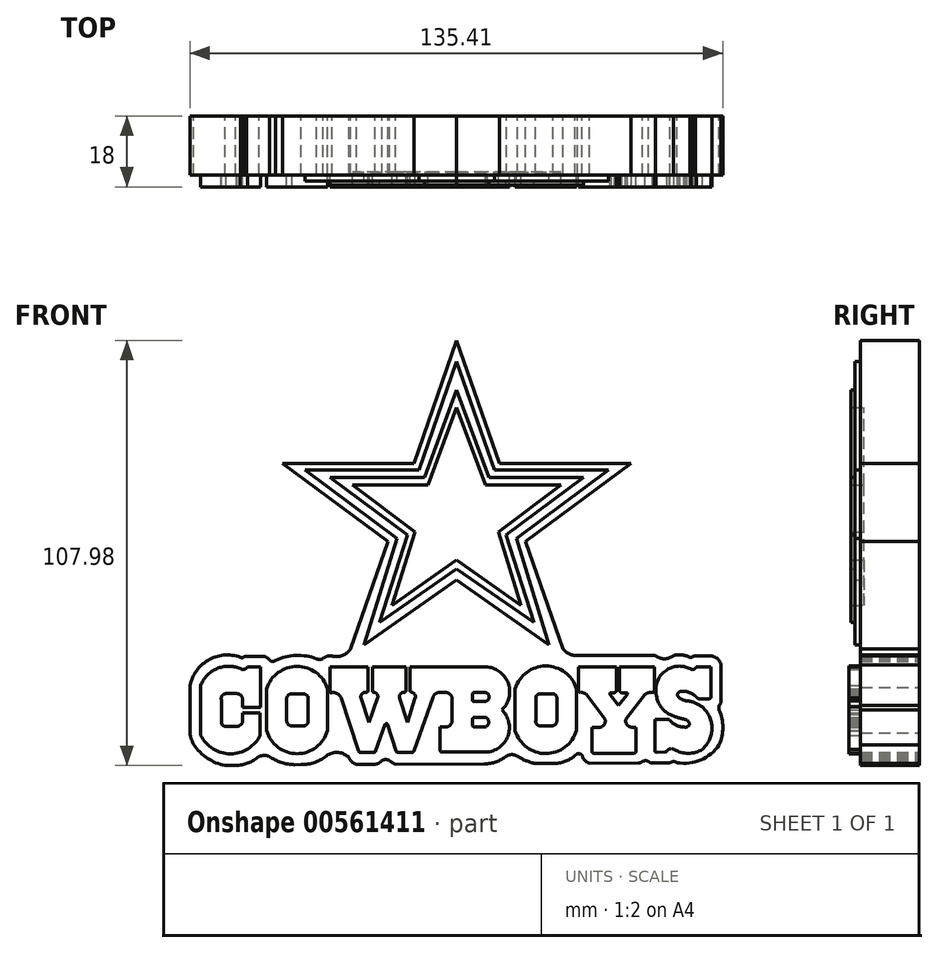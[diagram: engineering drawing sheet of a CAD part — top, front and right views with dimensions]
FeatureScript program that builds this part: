
annotation { "Feature Type Name" : "Feature", "Feature Type Description" : "" }
export const myFeature = defineFeature(function(context is Context, id is Id, definition is map)
    precondition{}
    {
        {
            var Q0;
            Q0=qCreatedBy(makeId("Front.planeOp"),FACE);
            var sketch = newSketch(context, id + "F0", { "sketchPlane" : qUnion([Q0])});
            skLineSegment(sketch, "E0", {"start": v(0, -3.42) * mm, "end": v(-16.39, -14.87) * mm});
            skLineSegment(sketch, "E1", {"start": v(-16.39, -14.87) * mm, "end": v(-10.6, 3.7) * mm});
            skLineSegment(sketch, "E2", {"start": v(-10.6, 3.7) * mm, "end": v(-26.52, 15.64) * mm});
            skLineSegment(sketch, "E3", {"start": v(-26.52, 15.64) * mm, "end": v(-7.34, 15.64) * mm});
            skLineSegment(sketch, "E4", {"start": v(-7.34, 15.64) * mm, "end": v(0, 35.41) * mm});
            skLineSegment(sketch, "E5.MirrorCS", {"start": v(7.34, 15.64) * mm, "end": v(0, 35.41) * mm});
            skLineSegment(sketch, "E6.MirrorCS", {"start": v(26.52, 15.64) * mm, "end": v(7.34, 15.64) * mm});
            skLineSegment(sketch, "E7.MirrorCS", {"start": v(10.6, 3.7) * mm, "end": v(26.52, 15.64) * mm});
            skLineSegment(sketch, "E8.MirrorCS", {"start": v(16.39, -14.87) * mm, "end": v(10.6, 3.7) * mm});
            skLineSegment(sketch, "E9.MirrorCS", {"start": v(0, -3.42) * mm, "end": v(16.39, -14.87) * mm});
            skSolve(sketch);
        }
        {
            var Q0;
            Q0=qCreatedBy(makeId("Front.planeOp"),FACE);
            var sketch = newSketch(context, id + "F1", { "sketchPlane" : qUnion([Q0])});
            skLineSegment(sketch, "E10", {"start": v(0, -5.59) * mm, "end": v(-19.65, -19.21) * mm});
            skLineSegment(sketch, "E11", {"start": v(-19.65, -19.21) * mm, "end": v(-12.53, 2.97) * mm});
            skLineSegment(sketch, "E12", {"start": v(-12.53, 2.97) * mm, "end": v(-32.19, 17.57) * mm});
            skLineSegment(sketch, "E13", {"start": v(-32.19, 17.57) * mm, "end": v(-8.19, 17.57) * mm});
            skLineSegment(sketch, "E14", {"start": v(-8.19, 17.57) * mm, "end": v(0, 39.88) * mm});
            skLineSegment(sketch, "E15.MirrorCS", {"start": v(8.19, 17.57) * mm, "end": v(0, 39.88) * mm});
            skLineSegment(sketch, "E16.MirrorCS", {"start": v(32.19, 17.57) * mm, "end": v(8.19, 17.57) * mm});
            skLineSegment(sketch, "E17.MirrorCS", {"start": v(12.53, 2.97) * mm, "end": v(32.19, 17.57) * mm});
            skLineSegment(sketch, "E18.MirrorCS", {"start": v(19.65, -19.21) * mm, "end": v(12.53, 2.97) * mm});
            skLineSegment(sketch, "E19.MirrorCS", {"start": v(0, -5.59) * mm, "end": v(19.65, -19.21) * mm});
            skSolve(sketch);
        }
        {
            var Q0;
            Q0=qCreatedBy(makeId("Front.planeOp"),FACE);
            var sketch = newSketch(context, id + "F2", { "sketchPlane" : qUnion([Q0])});
            skLineSegment(sketch, "E20", {"start": v(0, -8.48) * mm, "end": v(-23.5, -24.88) * mm});
            skLineSegment(sketch, "E21", {"start": v(-23.5, -24.88) * mm, "end": v(-15.18, 2.13) * mm});
            skLineSegment(sketch, "E22", {"start": v(-15.18, 2.13) * mm, "end": v(-38.58, 19.5) * mm});
            skLineSegment(sketch, "E23", {"start": v(-38.58, 19.5) * mm, "end": v(-9.64, 19.5) * mm});
            skLineSegment(sketch, "E24", {"start": v(-9.64, 19.5) * mm, "end": v(0, 47.11) * mm});
            skLineSegment(sketch, "E25.MirrorCS", {"start": v(9.64, 19.5) * mm, "end": v(0, 47.11) * mm});
            skLineSegment(sketch, "E26.MirrorCS", {"start": v(38.58, 19.5) * mm, "end": v(9.64, 19.5) * mm});
            skLineSegment(sketch, "E27.MirrorCS", {"start": v(15.18, 2.13) * mm, "end": v(38.58, 19.5) * mm});
            skLineSegment(sketch, "E28.MirrorCS", {"start": v(23.5, -24.88) * mm, "end": v(15.18, 2.13) * mm});
            skLineSegment(sketch, "E29.MirrorCS", {"start": v(0, -8.48) * mm, "end": v(23.5, -24.88) * mm});
            skSolve(sketch);
        }
        {
            var Q0;
            Q0=qCreatedBy(makeId("Front.planeOp"),FACE);
            var sketch = newSketch(context, id + "F3", { "sketchPlane" : qUnion([Q0])});
            skLineSegment(sketch, "E30", {"start": v(-17.47, 1.4) * mm, "end": v(-44.25, 21.18) * mm});
            skLineSegment(sketch, "E31", {"start": v(-44.25, 21.18) * mm, "end": v(-10.84, 21.18) * mm});
            skLineSegment(sketch, "E32", {"start": v(-10.84, 21.18) * mm, "end": v(0, 52.42) * mm});
            skLineSegment(sketch, "E33.MirrorCS", {"start": v(10.84, 21.18) * mm, "end": v(0, 52.42) * mm});
            skLineSegment(sketch, "E34.MirrorCS", {"start": v(44.25, 21.18) * mm, "end": v(10.84, 21.18) * mm});
            skLineSegment(sketch, "E35.MirrorCS", {"start": v(17.47, 1.4) * mm, "end": v(44.25, 21.18) * mm});
            skLineSegment(sketch, "E36", {"start": v(-17.47, 1.4) * mm, "end": v(-26.94, -25.93) * mm});
            skLineSegment(sketch, "E37", {"start": v(17.47, 1.4) * mm, "end": v(27.01, -25.93) * mm});
            skArc(sketch, "E38", {"start": v(-31.7, -27.78) * mm, "mid": v(-29.02, -27.61) * mm, "end": v(-26.94, -25.93) * mm});
            skArc(sketch, "E39", {"start": v(27.01, -25.93) * mm, "mid": v(28.63, -27.25) * mm, "end": v(30.68, -27.61) * mm});
            skPoint(sketch, "E39.endSnap0", {"position": v(-29.02, -27.61) * mm});
            skLineSegment(sketch, "E40", {"start": v(30.68, -27.61) * mm, "end": v(50.53, -27.61) * mm});
            skArc(sketch, "E41", {"start": v(50.53, -27.61) * mm, "mid": v(52.77, -28.5) * mm, "end": v(55.02, -27.61) * mm});
            skArc(sketch, "E42", {"start": v(59.28, -28.07) * mm, "mid": v(57.19, -27.52) * mm, "end": v(55.02, -27.61) * mm});
            skArc(sketch, "E43", {"start": v(59.28, -28.07) * mm, "mid": v(59.5, -28.14) * mm, "end": v(59.73, -28.07) * mm});
            skArc(sketch, "E44", {"start": v(60.66, -27.75) * mm, "mid": v(60.17, -27.83) * mm, "end": v(59.73, -28.07) * mm});
            skLineSegment(sketch, "E45", {"start": v(60.66, -27.75) * mm, "end": v(64.91, -27.75) * mm});
            skArc(sketch, "E46", {"start": v(67.17, -29.98) * mm, "mid": v(66.35, -28.55) * mm, "end": v(64.91, -27.75) * mm});
            skLineSegment(sketch, "E47", {"start": v(67.17, -29.98) * mm, "end": v(67.17, -39.09) * mm});
            skArc(sketch, "E48", {"start": v(66.68, -40.34) * mm, "mid": v(67.05, -39.76) * mm, "end": v(67.17, -39.09) * mm});
            skArc(sketch, "E49", {"start": v(66.68, -40.34) * mm, "mid": v(66.58, -40.9) * mm, "end": v(66.68, -41.47) * mm});
            skArc(sketch, "E50", {"start": v(66.68, -50.32) * mm, "mid": v(67.6, -45.9) * mm, "end": v(66.68, -41.47) * mm});
            skArc(sketch, "E51", {"start": v(56, -54.86) * mm, "mid": v(55.12, -54.58) * mm, "end": v(54.23, -54.86) * mm});
            skLineSegment(sketch, "E52", {"start": v(53.72, -54.97) * mm, "end": v(53.27, -54.97) * mm});
            skLineSegment(sketch, "E53", {"start": v(49.73, -54.97) * mm, "end": v(53.27, -54.97) * mm});
            skArc(sketch, "E54", {"start": v(53.72, -54.97) * mm, "mid": v(53.98, -54.94) * mm, "end": v(54.23, -54.86) * mm});
            skArc(sketch, "E55", {"start": v(48.7, -54.54) * mm, "mid": v(49.17, -54.86) * mm, "end": v(49.73, -54.97) * mm});
            skArc(sketch, "E56", {"start": v(48.7, -54.54) * mm, "mid": v(47.97, -54.35) * mm, "end": v(47.24, -54.54) * mm});
            skArc(sketch, "E57", {"start": v(46.16, -54.97) * mm, "mid": v(46.74, -54.86) * mm, "end": v(47.24, -54.54) * mm});
            skArc(sketch, "E58", {"start": v(56, -54.86) * mm, "mid": v(62.02, -54.19) * mm, "end": v(66.68, -50.32) * mm});
            skLineSegment(sketch, "E59", {"start": v(46.16, -54.97) * mm, "end": v(33.8, -55.02) * mm});
            skArc(sketch, "E60", {"start": v(31.88, -53.01) * mm, "mid": v(32.55, -54.3) * mm, "end": v(33.8, -55.02) * mm});
            skArc(sketch, "E61", {"start": v(31.88, -53.01) * mm, "mid": v(31, -52.57) * mm, "end": v(30.1, -53.01) * mm});
            skArc(sketch, "E62", {"start": v(24.4, -55.07) * mm, "mid": v(27.45, -54.58) * mm, "end": v(30.1, -53.01) * mm});
            skLineSegment(sketch, "E63", {"start": v(24.4, -55.07) * mm, "end": v(20, -55.09) * mm});
            skArc(sketch, "E64", {"start": v(15.4, -53.18) * mm, "mid": v(17.6, -54.36) * mm, "end": v(20, -55.09) * mm});
            skArc(sketch, "E65", {"start": v(15.4, -53.18) * mm, "mid": v(14.02, -52.8) * mm, "end": v(12.65, -53.18) * mm});
            skArc(sketch, "E66", {"start": v(7.07, -55.14) * mm, "mid": v(10.03, -54.64) * mm, "end": v(12.65, -53.18) * mm});
            skLineSegment(sketch, "E67", {"start": v(7.07, -55.14) * mm, "end": v(-15.54, -55.25) * mm});
            skArc(sketch, "E68", {"start": v(-17.1, -54.3) * mm, "mid": v(-16.37, -54.84) * mm, "end": v(-15.54, -55.25) * mm});
            skArc(sketch, "E69", {"start": v(-17.1, -54.3) * mm, "mid": v(-18.04, -54.07) * mm, "end": v(-18.97, -54.3) * mm});
            skArc(sketch, "E70", {"start": v(-20.76, -55.27) * mm, "mid": v(-19.77, -54.96) * mm, "end": v(-18.97, -54.3) * mm});
            skLineSegment(sketch, "E71", {"start": v(-20.76, -55.27) * mm, "end": v(-25.43, -55.3) * mm});
            skArc(sketch, "E72", {"start": v(-27.35, -53.58) * mm, "mid": v(-26.61, -54.69) * mm, "end": v(-25.43, -55.3) * mm});
            skArc(sketch, "E73", {"start": v(-27.35, -53.58) * mm, "mid": v(-29.97, -52.3) * mm, "end": v(-32.81, -52.93) * mm});
            skArc(sketch, "E74", {"start": v(-39.54, -55.36) * mm, "mid": v(-35.95, -54.76) * mm, "end": v(-32.81, -52.93) * mm});
            skLineSegment(sketch, "E75", {"start": v(-39.54, -55.36) * mm, "end": v(-41.14, -55.36) * mm});
            skArc(sketch, "E76", {"start": v(-47.66, -53.22) * mm, "mid": v(-44.57, -54.82) * mm, "end": v(-41.14, -55.36) * mm});
            skArc(sketch, "E77", {"start": v(-47.66, -53.22) * mm, "mid": v(-48.95, -53.04) * mm, "end": v(-50.23, -53.32) * mm});
            skArc(sketch, "E78", {"start": v(-56.17, -55.53) * mm, "mid": v(-53, -54.97) * mm, "end": v(-50.23, -53.32) * mm});
            skLineSegment(sketch, "E79", {"start": v(-56.17, -55.53) * mm, "end": v(-58.84, -55.56) * mm});
            skArc(sketch, "E80", {"start": v(-66.8, -50.28) * mm, "mid": v(-63.35, -53.72) * mm, "end": v(-58.84, -55.56) * mm});
            skArc(sketch, "E81", {"start": v(-67.8, -47.25) * mm, "mid": v(-67.46, -48.82) * mm, "end": v(-66.8, -50.28) * mm});
            skLineSegment(sketch, "E82", {"start": v(-67.8, -47.25) * mm, "end": v(-67.8, -35.8) * mm});
            skArc(sketch, "E83", {"start": v(-54.95, -28.06) * mm, "mid": v(-63.21, -28.88) * mm, "end": v(-67.8, -35.8) * mm});
            skArc(sketch, "E84", {"start": v(-54.95, -28.06) * mm, "mid": v(-54.54, -28.2) * mm, "end": v(-54.14, -28.06) * mm});
            skArc(sketch, "E85", {"start": v(-53.34, -27.86) * mm, "mid": v(-53.76, -27.88) * mm, "end": v(-54.14, -28.06) * mm});
            skLineSegment(sketch, "E86", {"start": v(-53.34, -27.86) * mm, "end": v(-49.26, -27.86) * mm});
            skArc(sketch, "E87", {"start": v(-47.52, -28.86) * mm, "mid": v(-48.26, -28.13) * mm, "end": v(-49.26, -27.86) * mm});
            skArc(sketch, "E88", {"start": v(-47.52, -28.86) * mm, "mid": v(-46.76, -29.12) * mm, "end": v(-46, -28.86) * mm});
            skArc(sketch, "E89", {"start": v(-35.59, -28.46) * mm, "mid": v(-40.83, -27.63) * mm, "end": v(-46, -28.86) * mm});
            skArc(sketch, "E90", {"start": v(-35.59, -28.46) * mm, "mid": v(-34.8, -28.67) * mm, "end": v(-34.01, -28.46) * mm});
            skArc(sketch, "E91", {"start": v(-31.7, -27.78) * mm, "mid": v(-32.94, -27.84) * mm, "end": v(-34.01, -28.46) * mm});
            skSolve(sketch);
        }
        {
            var Q0;
            Q0=qCreatedBy(makeId("Front.planeOp"),FACE);
            var sketch = newSketch(context, id + "F4", { "sketchPlane" : qUnion([Q0])});
            skLineSegment(sketch, "E92", {"start": v(-49.84, -30.58) * mm, "end": v(-49.84, -40.76) * mm});
            skLineSegment(sketch, "E93", {"start": v(-49.84, -40.76) * mm, "end": v(-54.38, -40.76) * mm});
            skLineSegment(sketch, "E94", {"start": v(-54.38, -40.76) * mm, "end": v(-54.38, -38.81) * mm});
            skArc(sketch, "E95", {"start": v(-54.38, -38.81) * mm, "mid": v(-54.78, -37.79) * mm, "end": v(-55.77, -37.32) * mm});
            skLineSegment(sketch, "E96", {"start": v(-55.77, -37.32) * mm, "end": v(-58.57, -37.32) * mm});
            skArc(sketch, "E97", {"start": v(-58.57, -37.32) * mm, "mid": v(-59.54, -37.77) * mm, "end": v(-59.8, -38.81) * mm});
            skLineSegment(sketch, "E98", {"start": v(-59.8, -38.81) * mm, "end": v(-59.8, -44.55) * mm});
            skArc(sketch, "E99", {"start": v(-59.8, -44.55) * mm, "mid": v(-59.43, -45.37) * mm, "end": v(-58.57, -45.65) * mm});
            skArc(sketch, "E100", {"start": v(-55.96, -45.65) * mm, "mid": v(-55.01, -45.34) * mm, "end": v(-54.4, -44.55) * mm});
            skLineSegment(sketch, "E101", {"start": v(-58.57, -45.65) * mm, "end": v(-55.96, -45.65) * mm});
            skLineSegment(sketch, "E102", {"start": v(-54.4, -44.55) * mm, "end": v(-54.4, -42.24) * mm});
            skLineSegment(sketch, "E103", {"start": v(-54.4, -42.24) * mm, "end": v(-49.91, -42.24) * mm});
            skLineSegment(sketch, "E104", {"start": v(-49.91, -42.24) * mm, "end": v(-49.91, -47.9) * mm});
            skArc(sketch, "E105", {"start": v(-65.03, -47.9) * mm, "mid": v(-57.47, -52.6) * mm, "end": v(-49.91, -47.9) * mm});
            skLineSegment(sketch, "E106", {"start": v(-65.03, -47.9) * mm, "end": v(-65.03, -35.26) * mm});
            skArc(sketch, "E107", {"start": v(-55.05, -30.92) * mm, "mid": v(-60.96, -30.99) * mm, "end": v(-65.03, -35.26) * mm});
            skArc(sketch, "E108", {"start": v(-55.05, -30.92) * mm, "mid": v(-54.03, -31.16) * mm, "end": v(-53.17, -30.58) * mm});
            skLineSegment(sketch, "E109", {"start": v(-53.17, -30.58) * mm, "end": v(-49.84, -30.58) * mm});
            skLineSegment(sketch, "E110", {"start": v(-48.28, -46.68) * mm, "end": v(-48.28, -36.06) * mm});
            skArc(sketch, "E111", {"start": v(-32.8, -36.06) * mm, "mid": v(-40.54, -30.42) * mm, "end": v(-48.28, -36.06) * mm});
            skArc(sketch, "E112", {"start": v(-48.28, -46.68) * mm, "mid": v(-40.54, -52.58) * mm, "end": v(-32.8, -46.68) * mm});
            skLineSegment(sketch, "E113", {"start": v(-32.8, -46.68) * mm, "end": v(-32.8, -36.06) * mm});
            skLineSegment(sketch, "E114", {"start": v(-32.23, -30.58) * mm, "end": v(-22.56, -30.58) * mm});
            skLineSegment(sketch, "E115", {"start": v(-22.56, -30.58) * mm, "end": v(-22.56, -36.77) * mm});
            skLineSegment(sketch, "E116", {"start": v(-32.23, -30.58) * mm, "end": v(-32.23, -36.77) * mm});
            skArc(sketch, "E117", {"start": v(-32.23, -36.77) * mm, "mid": v(-32.08, -37.05) * mm, "end": v(-31.77, -37.07) * mm});
            skArc(sketch, "E118", {"start": v(-29.44, -38.25) * mm, "mid": v(-30.41, -37.27) * mm, "end": v(-31.77, -37.07) * mm});
            skLineSegment(sketch, "E119", {"start": v(-29.44, -38.25) * mm, "end": v(-24.96, -51.88) * mm});
            skArc(sketch, "E120", {"start": v(-24.96, -51.88) * mm, "mid": v(-24.77, -52.16) * mm, "end": v(-24.46, -52.28) * mm});
            skLineSegment(sketch, "E121", {"start": v(-24.46, -52.28) * mm, "end": v(-21.12, -52.28) * mm});
            skArc(sketch, "E122", {"start": v(-21.12, -52.28) * mm, "mid": v(-20.78, -52.17) * mm, "end": v(-20.57, -51.88) * mm});
            skLineSegment(sketch, "E123", {"start": v(-20.57, -51.88) * mm, "end": v(-18.15, -45.12) * mm});
            skArc(sketch, "E124", {"start": v(-17.6, -45.12) * mm, "mid": v(-17.87, -44.93) * mm, "end": v(-18.15, -45.12) * mm});
            skLineSegment(sketch, "E125", {"start": v(-17.6, -45.12) * mm, "end": v(-15.45, -51.88) * mm});
            skArc(sketch, "E126", {"start": v(-15.45, -51.88) * mm, "mid": v(-15.3, -52.13) * mm, "end": v(-15.04, -52.28) * mm});
            skLineSegment(sketch, "E127", {"start": v(-15.04, -52.28) * mm, "end": v(-11.39, -52.28) * mm});
            skArc(sketch, "E128", {"start": v(-11.39, -52.28) * mm, "mid": v(-11.06, -52.17) * mm, "end": v(-10.87, -51.88) * mm});
            skArc(sketch, "E129", {"start": v(-23.1, -36.99) * mm, "mid": v(-22.8, -36.96) * mm, "end": v(-22.56, -36.77) * mm});
            skArc(sketch, "E130", {"start": v(-23.1, -36.99) * mm, "mid": v(-24.1, -37.4) * mm, "end": v(-24.33, -38.47) * mm});
            skLineSegment(sketch, "E131", {"start": v(-24.33, -38.47) * mm, "end": v(-22.25, -44.58) * mm});
            skLineSegment(sketch, "E132", {"start": v(-22.25, -44.58) * mm, "end": v(-20.1, -38.47) * mm});
            skArc(sketch, "E133", {"start": v(-20.1, -38.47) * mm, "mid": v(-20.18, -37.52) * mm, "end": v(-20.97, -36.99) * mm});
            skArc(sketch, "E134", {"start": v(-21.4, -36.77) * mm, "mid": v(-21.21, -36.95) * mm, "end": v(-20.97, -36.99) * mm});
            skLineSegment(sketch, "E135", {"start": v(-21.4, -36.77) * mm, "end": v(-21.4, -30.55) * mm});
            skLineSegment(sketch, "E136", {"start": v(-21.4, -30.55) * mm, "end": v(-12.94, -30.55) * mm});
            skLineSegment(sketch, "E137", {"start": v(-12.94, -30.55) * mm, "end": v(-12.94, -36.77) * mm});
            skArc(sketch, "E138", {"start": v(-13.38, -36.99) * mm, "mid": v(-13.13, -36.94) * mm, "end": v(-12.94, -36.77) * mm});
            skArc(sketch, "E139", {"start": v(-13.38, -36.99) * mm, "mid": v(-14.33, -37.44) * mm, "end": v(-14.55, -38.47) * mm});
            skLineSegment(sketch, "E140", {"start": v(-14.55, -38.47) * mm, "end": v(-12.55, -44.58) * mm});
            skLineSegment(sketch, "E141", {"start": v(-12.55, -44.58) * mm, "end": v(-10.55, -38.47) * mm});
            skArc(sketch, "E142", {"start": v(-10.55, -38.47) * mm, "mid": v(-10.62, -37.56) * mm, "end": v(-11.33, -36.99) * mm});
            skArc(sketch, "E143", {"start": v(-11.8, -36.77) * mm, "mid": v(-11.59, -36.93) * mm, "end": v(-11.33, -36.99) * mm});
            skLineSegment(sketch, "E144", {"start": v(-11.8, -36.77) * mm, "end": v(-11.8, -30.55) * mm});
            skLineSegment(sketch, "E145", {"start": v(-11.8, -30.55) * mm, "end": v(7.82, -30.55) * mm});
            skArc(sketch, "E146", {"start": v(11.47, -41.43) * mm, "mid": v(13.14, -34.82) * mm, "end": v(7.82, -30.55) * mm});
            skArc(sketch, "E147", {"start": v(7.44, -52.18) * mm, "mid": v(12.98, -48.13) * mm, "end": v(11.47, -41.43) * mm});
            skLineSegment(sketch, "E148", {"start": v(7.44, -52.18) * mm, "end": v(-3.7, -52.18) * mm});
            skArc(sketch, "E149", {"start": v(-4.21, -51.9) * mm, "mid": v(-4, -52.1) * mm, "end": v(-3.7, -52.18) * mm});
            skLineSegment(sketch, "E150", {"start": v(-4.21, -51.9) * mm, "end": v(-4.21, -45.8) * mm});
            skLineSegment(sketch, "E151", {"start": v(-4.21, -45.8) * mm, "end": v(-2.4, -45.8) * mm});
            skArc(sketch, "E152", {"start": v(-2.4, -45.8) * mm, "mid": v(-1.53, -45.18) * mm, "end": v(-1.17, -44.17) * mm});
            skLineSegment(sketch, "E153", {"start": v(-1.17, -44.17) * mm, "end": v(-1.17, -38.32) * mm});
            skArc(sketch, "E154", {"start": v(-1.17, -38.32) * mm, "mid": v(-1.7, -37.46) * mm, "end": v(-2.6, -37.03) * mm});
            skLineSegment(sketch, "E155", {"start": v(-2.6, -37.03) * mm, "end": v(-4.62, -37.03) * mm});
            skArc(sketch, "E156", {"start": v(-4.62, -37.03) * mm, "mid": v(-5.49, -37.45) * mm, "end": v(-6.03, -38.24) * mm});
            skLineSegment(sketch, "E157", {"start": v(-6.03, -38.24) * mm, "end": v(-10.87, -51.88) * mm});
            skLineSegment(sketch, "E158", {"start": v(3.99, -38.96) * mm, "end": v(3.99, -37.35) * mm});
            skArc(sketch, "E159", {"start": v(3.99, -38.96) * mm, "mid": v(4.22, -39.26) * mm, "end": v(4.59, -39.34) * mm});
            skArc(sketch, "E160", {"start": v(4.59, -37.02) * mm, "mid": v(4.23, -37.08) * mm, "end": v(3.99, -37.35) * mm});
            skLineSegment(sketch, "E161", {"start": v(4.59, -37.02) * mm, "end": v(7.32, -37.02) * mm});
            skArc(sketch, "E162", {"start": v(7.32, -39.32) * mm, "mid": v(8.21, -38.17) * mm, "end": v(7.32, -37.02) * mm});
            skLineSegment(sketch, "E163", {"start": v(7.32, -39.32) * mm, "end": v(4.59, -39.34) * mm});
            skLineSegment(sketch, "E164", {"start": v(4.59, -43.36) * mm, "end": v(7.32, -43.34) * mm});
            skArc(sketch, "E165", {"start": v(7.32, -45.76) * mm, "mid": v(8.15, -44.55) * mm, "end": v(7.32, -43.34) * mm});
            skArc(sketch, "E166", {"start": v(4.59, -43.36) * mm, "mid": v(4.25, -43.47) * mm, "end": v(4.03, -43.77) * mm});
            skLineSegment(sketch, "E167", {"start": v(4.03, -43.77) * mm, "end": v(4.03, -45.48) * mm});
            skArc(sketch, "E168", {"start": v(4.03, -45.48) * mm, "mid": v(4.27, -45.72) * mm, "end": v(4.6, -45.76) * mm});
            skLineSegment(sketch, "E169", {"start": v(4.6, -45.76) * mm, "end": v(7.32, -45.76) * mm});
            skLineSegment(sketch, "E170", {"start": v(-43.18, -44.19) * mm, "end": v(-43.18, -38.42) * mm});
            skArc(sketch, "E171", {"start": v(-41.86, -37.35) * mm, "mid": v(-42.72, -37.65) * mm, "end": v(-43.18, -38.42) * mm});
            skLineSegment(sketch, "E172", {"start": v(-41.86, -37.35) * mm, "end": v(-39.03, -37.35) * mm});
            skArc(sketch, "E173", {"start": v(-37.71, -38.42) * mm, "mid": v(-38.18, -37.65) * mm, "end": v(-39.03, -37.35) * mm});
            skArc(sketch, "E174", {"start": v(-43.18, -44.19) * mm, "mid": v(-42.8, -45.13) * mm, "end": v(-41.86, -45.53) * mm});
            skLineSegment(sketch, "E175", {"start": v(-41.86, -45.53) * mm, "end": v(-39.03, -45.55) * mm});
            skArc(sketch, "E176", {"start": v(-39.03, -45.55) * mm, "mid": v(-38.08, -45.15) * mm, "end": v(-37.71, -44.19) * mm});
            skLineSegment(sketch, "E177", {"start": v(-37.71, -44.19) * mm, "end": v(-37.71, -38.42) * mm});
            skArc(sketch, "E178", {"start": v(14.87, -46.75) * mm, "mid": v(22.67, -52.55) * mm, "end": v(30.42, -46.68) * mm});
            skArc(sketch, "E179", {"start": v(30.42, -36.06) * mm, "mid": v(22.65, -30.3) * mm, "end": v(14.87, -36.06) * mm});
            skLineSegment(sketch, "E180", {"start": v(14.87, -46.75) * mm, "end": v(14.87, -36.06) * mm});
            skLineSegment(sketch, "E181", {"start": v(30.42, -36.06) * mm, "end": v(30.42, -46.68) * mm});
            skLineSegment(sketch, "E182", {"start": v(40.62, -36.42) * mm, "end": v(40.62, -30.56) * mm});
            skLineSegment(sketch, "E183", {"start": v(40.62, -30.56) * mm, "end": v(30.9, -30.56) * mm});
            skLineSegment(sketch, "E184", {"start": v(30.9, -30.56) * mm, "end": v(30.9, -36.42) * mm});
            skArc(sketch, "E185", {"start": v(30.9, -36.42) * mm, "mid": v(31.07, -36.87) * mm, "end": v(31.49, -37.1) * mm});
            skArc(sketch, "E186", {"start": v(40.09, -37.1) * mm, "mid": v(40.47, -36.85) * mm, "end": v(40.62, -36.42) * mm});
            skArc(sketch, "E187", {"start": v(33, -37.58) * mm, "mid": v(32.3, -37.14) * mm, "end": v(31.49, -37.1) * mm});
            skArc(sketch, "E188", {"start": v(39.28, -37.1) * mm, "mid": v(38.94, -37.22) * mm, "end": v(38.96, -37.58) * mm});
            skLineSegment(sketch, "E189", {"start": v(39.28, -37.1) * mm, "end": v(40.09, -37.1) * mm});
            skLineSegment(sketch, "E190", {"start": v(38.96, -37.58) * mm, "end": v(41.07, -40.28) * mm});
            skLineSegment(sketch, "E191", {"start": v(41.07, -40.28) * mm, "end": v(43.3, -37.63) * mm});
            skLineSegment(sketch, "E192", {"start": v(43.3, -37.63) * mm, "end": v(43.34, -37.58) * mm});
            skArc(sketch, "E193", {"start": v(43.34, -37.58) * mm, "mid": v(43.37, -37.26) * mm, "end": v(43.1, -37.1) * mm});
            skArc(sketch, "E194", {"start": v(41.39, -36.42) * mm, "mid": v(41.54, -36.91) * mm, "end": v(42.01, -37.1) * mm});
            skLineSegment(sketch, "E195", {"start": v(42.01, -37.1) * mm, "end": v(43.1, -37.1) * mm});
            skLineSegment(sketch, "E196", {"start": v(41.39, -36.42) * mm, "end": v(41.39, -30.56) * mm});
            skLineSegment(sketch, "E197", {"start": v(41.39, -30.56) * mm, "end": v(50.23, -30.56) * mm});
            skLineSegment(sketch, "E198", {"start": v(50.23, -30.56) * mm, "end": v(50.23, -36.42) * mm});
            skArc(sketch, "E199", {"start": v(49.68, -37.1) * mm, "mid": v(50.08, -36.86) * mm, "end": v(50.23, -36.42) * mm});
            skArc(sketch, "E200", {"start": v(49.68, -37.1) * mm, "mid": v(48.7, -37.1) * mm, "end": v(47.84, -37.58) * mm});
            skLineSegment(sketch, "E201", {"start": v(33, -37.58) * mm, "end": v(37.59, -43.62) * mm});
            skLineSegment(sketch, "E202", {"start": v(47.84, -37.58) * mm, "end": v(43.07, -43.62) * mm});
            skArc(sketch, "E203", {"start": v(36.51, -45.85) * mm, "mid": v(37.6, -45) * mm, "end": v(37.59, -43.62) * mm});
            skArc(sketch, "E204", {"start": v(43.07, -43.62) * mm, "mid": v(43.15, -45.07) * mm, "end": v(44.4, -45.85) * mm});
            skLineSegment(sketch, "E205", {"start": v(36.51, -45.85) * mm, "end": v(34.4, -45.85) * mm});
            skLineSegment(sketch, "E206", {"start": v(34.4, -45.85) * mm, "end": v(34.4, -52.06) * mm});
            skArc(sketch, "E207", {"start": v(34.4, -52.06) * mm, "mid": v(34.54, -52.36) * mm, "end": v(34.86, -52.45) * mm});
            skLineSegment(sketch, "E208", {"start": v(34.86, -52.45) * mm, "end": v(45.06, -52.45) * mm});
            skArc(sketch, "E209", {"start": v(45.06, -52.45) * mm, "mid": v(45.37, -52.34) * mm, "end": v(45.56, -52.06) * mm});
            skLineSegment(sketch, "E210", {"start": v(45.56, -52.06) * mm, "end": v(45.56, -45.85) * mm});
            skLineSegment(sketch, "E211", {"start": v(45.56, -45.85) * mm, "end": v(44.4, -45.85) * mm});
            skLineSegment(sketch, "E212", {"start": v(64.57, -38.35) * mm, "end": v(64.57, -30.54) * mm});
            skLineSegment(sketch, "E213", {"start": v(64.57, -30.54) * mm, "end": v(60.87, -30.54) * mm});
            skArc(sketch, "E214", {"start": v(59.45, -31.1) * mm, "mid": v(60.29, -31.14) * mm, "end": v(60.87, -30.54) * mm});
            skArc(sketch, "E215", {"start": v(59.45, -31.1) * mm, "mid": v(56.58, -30.34) * mm, "end": v(53.7, -31.1) * mm});
            skArc(sketch, "E216", {"start": v(53.7, -31.1) * mm, "mid": v(51.09, -34) * mm, "end": v(50.77, -37.89) * mm});
            skArc(sketch, "E217", {"start": v(50.77, -37.89) * mm, "mid": v(51.87, -40.68) * mm, "end": v(54.15, -42.62) * mm});
            skArc(sketch, "E218", {"start": v(54.15, -42.62) * mm, "mid": v(56.13, -43.35) * mm, "end": v(58.17, -43.92) * mm});
            skArc(sketch, "E219", {"start": v(54.02, -43.87) * mm, "mid": v(55.65, -45.31) * mm, "end": v(57.77, -45.8) * mm});
            skArc(sketch, "E220", {"start": v(59.12, -45.15) * mm, "mid": v(58.84, -44.38) * mm, "end": v(58.17, -43.92) * mm});
            skArc(sketch, "E221", {"start": v(57.77, -45.8) * mm, "mid": v(58.57, -45.75) * mm, "end": v(59.12, -45.15) * mm});
            skLineSegment(sketch, "E222", {"start": v(54.02, -43.87) * mm, "end": v(50.31, -43.87) * mm});
            skLineSegment(sketch, "E223", {"start": v(50.31, -43.87) * mm, "end": v(50.31, -51.8) * mm});
            skArc(sketch, "E224", {"start": v(50.31, -51.8) * mm, "mid": v(50.42, -52.08) * mm, "end": v(50.7, -52.19) * mm});
            skLineSegment(sketch, "E225", {"start": v(50.7, -52.19) * mm, "end": v(52.95, -52.17) * mm});
            skArc(sketch, "E226", {"start": v(52.95, -52.17) * mm, "mid": v(53.24, -52.1) * mm, "end": v(53.47, -51.9) * mm});
            skArc(sketch, "E227", {"start": v(55.23, -51.44) * mm, "mid": v(54.26, -51.34) * mm, "end": v(53.47, -51.9) * mm});
            skArc(sketch, "E228", {"start": v(55.23, -51.44) * mm, "mid": v(58.83, -52.47) * mm, "end": v(62.42, -51.44) * mm});
            skArc(sketch, "E229", {"start": v(62.42, -51.44) * mm, "mid": v(64.88, -46.1) * mm, "end": v(62.42, -40.74) * mm});
            skArc(sketch, "E230", {"start": v(62.42, -40.74) * mm, "mid": v(60.58, -39.67) * mm, "end": v(58.52, -39.15) * mm});
            skArc(sketch, "E231", {"start": v(56.26, -38.07) * mm, "mid": v(57.29, -38.83) * mm, "end": v(58.52, -39.15) * mm});
            skArc(sketch, "E232", {"start": v(56.76, -36.79) * mm, "mid": v(56.2, -37.3) * mm, "end": v(56.26, -38.07) * mm});
            skArc(sketch, "E233", {"start": v(60.23, -37.65) * mm, "mid": v(58.58, -36.86) * mm, "end": v(56.76, -36.79) * mm});
            skArc(sketch, "E234", {"start": v(61.21, -38.53) * mm, "mid": v(60.74, -38.07) * mm, "end": v(60.23, -37.65) * mm});
            skLineSegment(sketch, "E235", {"start": v(61.63, -38.64) * mm, "end": v(63.98, -38.64) * mm});
            skArc(sketch, "E236", {"start": v(63.98, -38.64) * mm, "mid": v(64.3, -38.56) * mm, "end": v(64.57, -38.35) * mm});
            skArc(sketch, "E237", {"start": v(61.21, -38.53) * mm, "mid": v(61.41, -38.61) * mm, "end": v(61.63, -38.64) * mm});
            skArc(sketch, "E238", {"start": v(20.09, -44.19) * mm, "mid": v(20.34, -45.12) * mm, "end": v(21.21, -45.52) * mm});
            skArc(sketch, "E239", {"start": v(24.26, -45.52) * mm, "mid": v(25.12, -45.1) * mm, "end": v(25.44, -44.19) * mm});
            skLineSegment(sketch, "E240", {"start": v(21.21, -45.52) * mm, "end": v(24.26, -45.52) * mm});
            skLineSegment(sketch, "E241", {"start": v(20.09, -44.19) * mm, "end": v(20.09, -38.41) * mm});
            skLineSegment(sketch, "E242", {"start": v(25.44, -44.19) * mm, "end": v(25.44, -38.41) * mm});
            skArc(sketch, "E243", {"start": v(25.44, -38.41) * mm, "mid": v(25.08, -37.63) * mm, "end": v(24.24, -37.4) * mm});
            skArc(sketch, "E244", {"start": v(21.2, -37.4) * mm, "mid": v(20.42, -37.66) * mm, "end": v(20.09, -38.41) * mm});
            skLineSegment(sketch, "E245", {"start": v(21.2, -37.4) * mm, "end": v(24.24, -37.4) * mm});
            skSolve(sketch);
        }
        {
            var Q0;
            Q0 = qSketchRegion(id + "F3", true);
            extrude(context, id + "F5", {"entities" : qUnion([Q0]), "depth" : 15 * mm, "offsetDistance" : 25 * mm});
        }
        {
            var Q0;
            Q0 = qSketchRegion(id + "F4", true);
            extrude(context, id + "F6", {"entities" : qUnion([Q0]), "operationType" : NewBodyOperationType.ADD, "depth" : 18 * mm, "offsetDistance" : 25 * mm});
        }
        {
            var Q0;
            Q0 = qSketchRegion(id + "F2", true);
            extrude(context, id + "F7", {"entities" : qUnion([Q0]), "operationType" : NewBodyOperationType.ADD, "depth" : 16.5 * mm, "offsetDistance" : 25 * mm});
        }
        {
            var Q0;
            Q0 = qSketchRegion(id + "F1", true);
            extrude(context, id + "F8", {"entities" : qUnion([Q0]), "operationType" : NewBodyOperationType.ADD, "depth" : 17.5 * mm, "offsetDistance" : 25 * mm});
        }
        {
            var Q0;
            Q0 = qSketchRegion(id + "F0", true);
            extrude(context, id + "F9", {"entities" : qUnion([Q0]), "operationType" : NewBodyOperationType.REMOVE, "depth" : 33.8 * mm, "offsetDistance" : 25 * mm, "hasSecondDirection" : true, "secondDirectionOppositeDirection" : false, "secondDirectionDepth" : 14.2 * mm});
        }
    });
